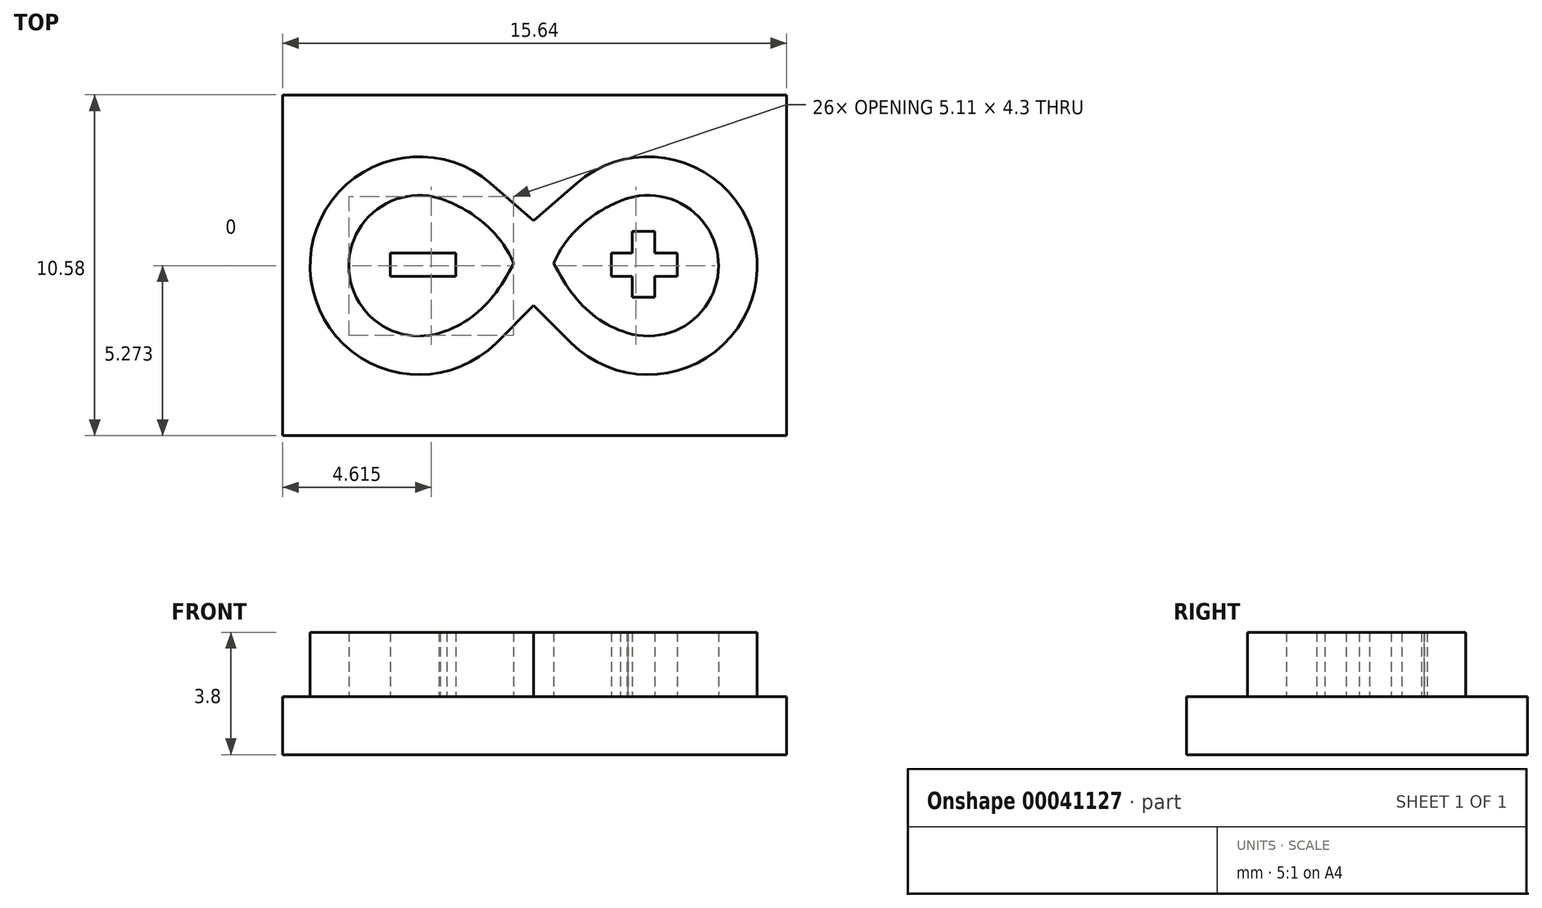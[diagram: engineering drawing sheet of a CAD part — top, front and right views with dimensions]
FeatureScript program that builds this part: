
annotation { "Feature Type Name" : "Feature", "Feature Type Description" : "" }
export const myFeature = defineFeature(function(context is Context, id is Id, definition is map)
    precondition{}
    {
        {
            var Q0;
            Q0=qCreatedBy(makeId("Top.planeOp"),FACE);
            var sketch = newSketch(context, id + "F0", { "sketchPlane" : qUnion([Q0])});
            skArc(sketch, "E0", {"start": v(5.1, 7.28) * mm, "mid": v(2.06, 5.38) * mm, "end": v(4.9, 3.2) * mm});
            skArc(sketch, "E1", {"start": v(6.46, 7.83) * mm, "mid": v(0.86, 5.16) * mm, "end": v(6.63, 2.88) * mm});
            skLineSegment(sketch, "E2", {"start": v(7.8, 4.04) * mm, "end": v(6.46, 2.7) * mm});
            skLineSegment(sketch, "E3", {"start": v(6.46, 2.7) * mm, "end": v(6.46, 2.72) * mm, "construction": true});
            skLineSegment(sketch, "E4", {"start": v(6.46, 7.83) * mm, "end": v(7.8, 6.67) * mm});
            skLineSegment(sketch, "E5.trimOffspring", {"start": v(9.12, 7.9) * mm, "end": v(9.12, 7.9) * mm});
            skPoint(sketch, "E6.endSnap0", {"position": v(7.8, 5.36) * mm});
            skLineSegment(sketch, "E7", {"start": v(8.47, 5.36) * mm, "end": v(8.41, 5.36) * mm, "construction": true});
            skPoint(sketch, "E7.endSnap0", {"position": v(8.13, 5.36) * mm});
            skFitSpline(sketch, "E8", {"points": [v(7.17, 5.36) * mm, v(4.86, 7.37) * mm, v(4.9, 7.36) * mm], "startDerivative": vector(-2.23, 5.2) * mm, "endDerivative": vector(0.49, -0.22) * mm});
            skFitSpline(sketch, "E9", {"points": [v(4.9, 3.2) * mm, v(7.17, 5.36) * mm], "startDerivative": vector(3.14, 0.96) * mm, "endDerivative": vector(1.64, 3.29) * mm});
            skLineSegment(sketch, "E10.bottom", {"start": v(3.34, 5.67) * mm, "end": v(5.38, 5.67) * mm});
            skLineSegment(sketch, "E10.top", {"start": v(3.34, 4.94) * mm, "end": v(5.38, 4.94) * mm});
            skLineSegment(sketch, "E10.left", {"start": v(3.34, 5.67) * mm, "end": v(3.34, 4.94) * mm});
            skLineSegment(sketch, "E10.right", {"start": v(5.38, 5.67) * mm, "end": v(5.38, 4.94) * mm});
            skArc(sketch, "E11.MirrorCS", {"start": v(9.13, 7.83) * mm, "mid": v(14.73, 5.16) * mm, "end": v(8.96, 2.88) * mm});
            skLineSegment(sketch, "E12.MirrorCS", {"start": v(12.25, 4.94) * mm, "end": v(11.55, 4.94) * mm});
            skLineSegment(sketch, "E13.MirrorCS", {"start": v(9.13, 7.83) * mm, "end": v(7.8, 6.67) * mm});
            skLineSegment(sketch, "E14.MirrorCS", {"start": v(12.25, 5.67) * mm, "end": v(12.25, 4.94) * mm});
            skFitSpline(sketch, "E15.MirrorCS", {"points": [v(8.41, 5.36) * mm, v(10.73, 7.37) * mm, v(10.7, 7.36) * mm], "startDerivative": vector(2.23, 5.2) * mm, "endDerivative": vector(-0.49, -0.22) * mm});
            skLineSegment(sketch, "E16.MirrorCS", {"start": v(7.8, 4.04) * mm, "end": v(9.13, 2.7) * mm});
            skPoint(sketch, "E17.MirrorP", {"position": v(7.46, 5.36) * mm});
            skLineSegment(sketch, "E18.MirrorCS", {"start": v(10.2, 5.67) * mm, "end": v(10.2, 4.94) * mm});
            skFitSpline(sketch, "E19.MirrorCS", {"points": [v(10.7, 3.2) * mm, v(8.41, 5.36) * mm], "startDerivative": vector(-3.14, 0.96) * mm, "endDerivative": vector(-1.64, 3.29) * mm});
            skLineSegment(sketch, "E20.MirrorCS", {"start": v(7.12, 5.36) * mm, "end": v(7.17, 5.36) * mm});
            skArc(sketch, "E21.MirrorCS", {"start": v(10.49, 7.28) * mm, "mid": v(13.53, 5.38) * mm, "end": v(10.7, 3.2) * mm});
            skLineSegment(sketch, "E22.bottom", {"start": v(10.86, 6.35) * mm, "end": v(11.55, 6.35) * mm});
            skLineSegment(sketch, "E22.top", {"start": v(10.86, 4.3) * mm, "end": v(11.55, 4.3) * mm});
            skLineSegment(sketch, "E22.left", {"start": v(10.86, 6.35) * mm, "end": v(10.86, 5.67) * mm});
            skLineSegment(sketch, "E22.right", {"start": v(11.55, 4.94) * mm, "end": v(11.55, 4.3) * mm});
            skLineSegment(sketch, "E23.trimOffspring", {"start": v(10.86, 4.94) * mm, "end": v(10.86, 4.3) * mm});
            skLineSegment(sketch, "E24.trimOffspring", {"start": v(10.86, 5.67) * mm, "end": v(10.2, 5.67) * mm});
            skLineSegment(sketch, "E25.trimOffspring", {"start": v(10.86, 4.94) * mm, "end": v(10.2, 4.94) * mm});
            skLineSegment(sketch, "E26", {"start": v(12.25, 5.67) * mm, "end": v(11.55, 5.67) * mm});
            skLineSegment(sketch, "E27", {"start": v(11.55, 5.67) * mm, "end": v(11.55, 6.35) * mm});
            skSolve(sketch);
        }
        {
            var Q0;
            Q0=makeQuery(id+"F0.imprint","IMPRINT",FACE,{"disambiguationData":[TD([[makeQuery(id+"F0.imprint","IMPRINT",EDGE,{"derivedFrom":sQuery(id+"F0.wireOp",EDGE,"E10.bottom")}),-1.0]])]});
            var Q1;
            {var subQ9=sQuery(id+"F0.wireOp",EDGE,"E1");Q1=makeQuery(id+"F0.imprint","IMPRINT",FACE,{"disambiguationData":[TD([[makeQuery(id+"F0.imprint","IMPRINT",EDGE,{"derivedFrom":subQ9}),1.0]])]});}
            var Q2;
            Q2=makeQuery(id+"F0.imprint","IMPRINT",FACE,{"disambiguationData":[TD([[makeQuery(id+"F0.imprint","IMPRINT",EDGE,{"derivedFrom":sQuery(id+"F0.wireOp",EDGE,"E12.MirrorCS")}),-1.0]])]});
            extrude(context, id + "F1", {"entities" : qUnion([Q0, Q1, Q2]), "depth" : 2 * mm});
        }
        {
            var Q0;
            Q0=qCreatedBy(makeId("Front.planeOp"),FACE);
            var sketch = newSketch(context, id + "F2", { "sketchPlane" : qUnion([Q0])});
            skLineSegment(sketch, "E28.bottom", {"start": v(0, 0) * mm, "end": v(15.64, 0) * mm});
            skLineSegment(sketch, "E28.top", {"start": v(0, -1.8) * mm, "end": v(15.64, -1.8) * mm});
            skLineSegment(sketch, "E28.left", {"start": v(0, 0) * mm, "end": v(0, -1.8) * mm});
            skLineSegment(sketch, "E28.right", {"start": v(15.64, 0) * mm, "end": v(15.64, -1.8) * mm});
            skSolve(sketch);
        }
        {
            var Q0;
            Q0=makeQuery(id+"F2.imprint","IMPRINT",FACE,{"disambiguationData":[TD([[makeQuery(id+"F2.imprint","IMPRINT",EDGE,{"derivedFrom":sQuery(id+"F2.wireOp",EDGE,"E28.bottom")}),-1.0]])]});
            extrude(context, id + "F3", {"entities" : qUnion([Q0]), "oppositeDirection" : true, "depth" : 10.58 * mm});
        }
    });
